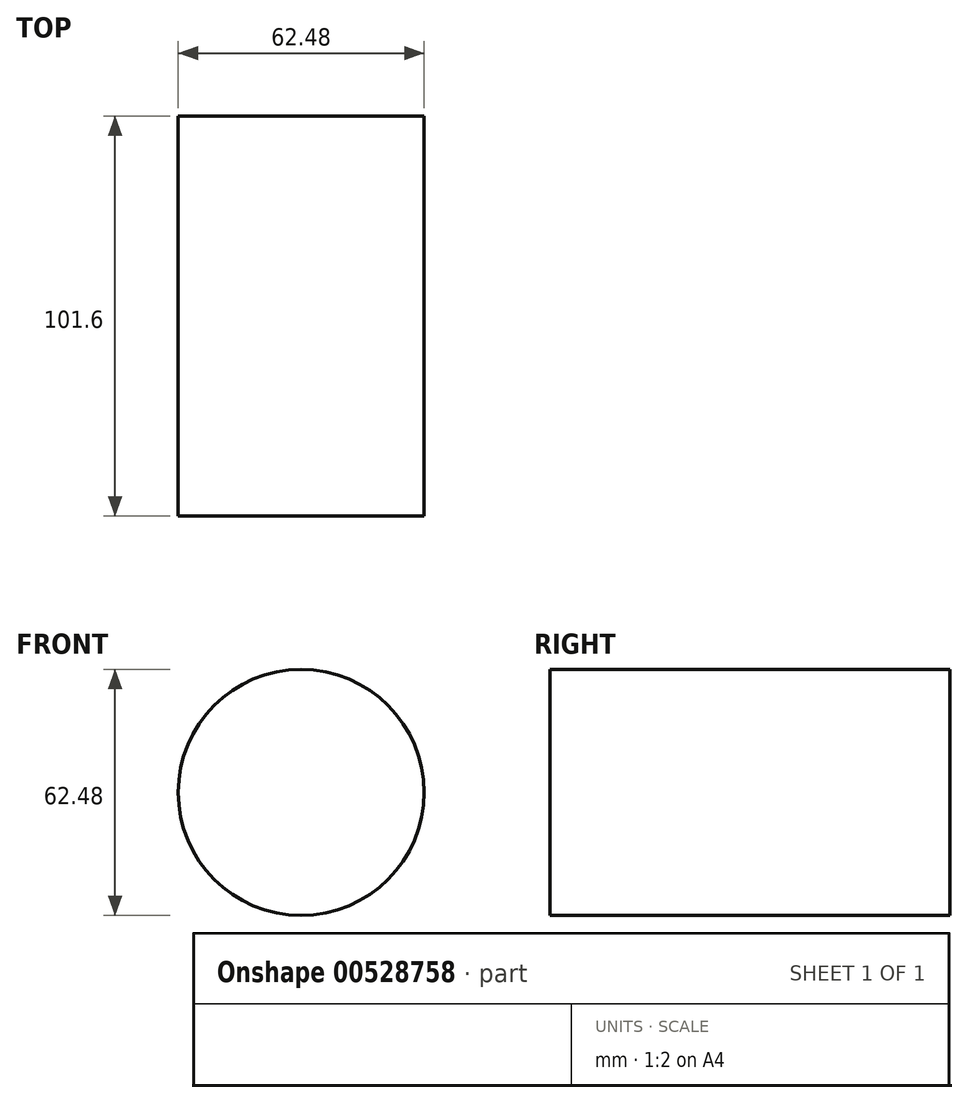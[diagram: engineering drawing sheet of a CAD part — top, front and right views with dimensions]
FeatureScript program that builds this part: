
annotation { "Feature Type Name" : "Feature", "Feature Type Description" : "" }
export const myFeature = defineFeature(function(context is Context, id is Id, definition is map)
    precondition{}
    {
        {
            var Q0;
            Q0=qCreatedBy(makeId("Front.planeOp"),FACE);
            var sketch = newSketch(context, id + "F0", { "sketchPlane" : qUnion([Q0])});
            skCircle(sketch, "E0", {"center": v(0, 0) * mm, "radius": 31.24 * mm});
            skSolve(sketch);
        }
        {
            var Q0;
            Q0 = qSketchRegion(id + "F0", true);
            extrude(context, id + "F1", {"entities" : qUnion([Q0]), "depth" : 25.4 * mm, "offsetDistance" : 25.4 * mm});
        }
        {
            var Q0;
            Q0=makeQuery(id+"F1.opExtrude","CAP_FACE",FACE,{"disambiguationData":[OSD([sQuery(id+"F0.wireOp",EDGE,"E0")])],"isStart":false});
            extrude(context, id + "F2", {"entities" : qUnion([Q0]), "operationType" : NewBodyOperationType.ADD, "depth" : 76.2 * mm, "offsetDistance" : 25.4 * mm});
        }
    });
